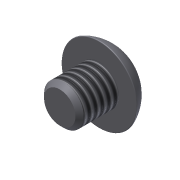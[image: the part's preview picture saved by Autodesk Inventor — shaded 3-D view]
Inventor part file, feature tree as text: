
AUTODESK INVENTOR PART (.ipt)
format: ipt  version: 2013 (Build 170138000, 138)  size: 131,072 bytes
history: native  units: in
note: dims shown in document units (in); Inventor stores cm internally (conversion verified against a paired STEP export)
features: sketch x3, extrude x2, revolve x1, chamfer x1, thread x1
ambient origin geometry x8: Origin, YZ Plane, XZ Plane, XY Plane, X Axis, Y Axis, Z Axis, Center Point
bodies: Solid1 (feature_tree)
feature tree (8):
  extrude  "Extrusion1"  Depth=0.188in TaperAngle=0.0deg
  revolve  "Revolution1"  [1 undecoded]
  extrude  "Extrusion2"  Depth=0.125in
  chamfer  "Chamfer1"  Distance=0.0625in
  thread  "Thread1"  [1 undecoded]
  sketch  "Sketch1"  dims[d0=0.19in d1=0.188in d2=0.0in]
  sketch  "Sketch2"  dims[d3=0.101in d6=0.08in]
  sketch  "Sketch3"  dims[d7=90.0deg d8=0.125in d9=0.0625in d10=0.0in d12=0.1805in d13=0.02in d14=0.125in d15=45.0deg d16=1.0in d17=0.0in d18=0.003in]
note: 2 required parameter values undecoded (feature->parameter linkage not recoverable at this tier; creation-order binding heuristic only, values carry confidence <= 0.55)